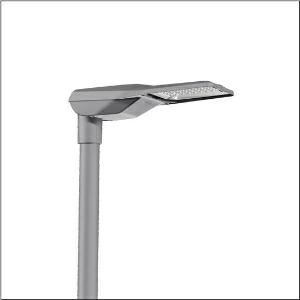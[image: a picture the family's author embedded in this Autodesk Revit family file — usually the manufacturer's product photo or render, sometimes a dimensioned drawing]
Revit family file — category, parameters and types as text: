
# Revit family: streetlight_sl_21_iq_mini___st1_0a_5xe2d31d08jb_a4dc
name_source: partatom
category: Lighting Fixtures
units: mm (PartAtom-declared; Revit-internal decimal feet)

## family parameters
Cut with Voids When Loaded = No
Host = Face
Light Source = No
Part Type = Normal
Room Calculation Point = No
Round Connector Dimension = Use Diameter
Shared = No

## types (1)
- --- (1 x LED, 10820 lm, 71.6 W, 3000K)
    Apparent Load = 72 VA
    CIE Flux Codes = 40 73 97 100 100
    Color Rendering = 70
    Color Temperature = 3000K
    Default Elevation = 1800 mm
    Description = Streetlight SL 21 iQ mini, mast luminaire, primary light control with lens, of PMMA, primary optical cover: cover, of toughened safety glass, transparent, light distribution: ST1.0a, light emission: direct distribution, primary light characteristic: asymmetric, installation type: post-top, side-entry, LED, High Power LED, rated luminous flux: 10.820lm, luminous efficacy: 151lm/W, light colour: 730, colour temperature: 3000K, control: Auto-Match, Temp-Guard, Lumen-Switch, Night-Set, Smart-Wire, Light-Fading, Desk-Remote (wireless, voltage-free reading and setting of iQ features in the workshop via application-optimized NFC function/RFID function), optimised constant luminous flux control (CLO 2.0), presetting dimming linear, mains connection: 220..240V, AC, 50/60Hz, start of lifetime: 72W, end of service life: 75W, reduction: 33W, luminaire housing, of diecast aluminium, powder-coated, Siteco® metallic grey (DB 702S), corrosivity category C5 mid according to DIN EN ISO 12944, please order mast flange separately, inclination adjustable: 0°, 5°, 10°, 15°, sealing non-destructively replaceable, multi-level sealing system, length: 628mm, width: 235mm, height: 110mm, mast flange for spigot size: 42mm (side-entry): 5XC10008XM4, 60/48mm (side-entry/post-top): 5XC10108XM2, 76/60mm (side-entry/post-top): 5XC10108XM1, protection rating (complete): IP66, insulation class (complete): insulation class II (safety insulation), certification: CE, ENEC, ENEC+, VDE, impact resistance: IK09, permissible operating ambient temperature for outdoor applications: -40..+50°C, standard-compliant lighting for roads and squares, packaging unit: 1 piece

Light Distribution: ST1.0a
    Height = 110 mm
    Lamp = 1 x LED
    Lamp Light Flux = 10820 lm
    Lamp Power = 71.6 W
    Lamp count = 1
    Length = 625 mm
    Luminous efficacy = 151 lm/W
    Manufacturer = Siteco
    ModVariant = No
    Model = 5XE2D31D08JB
    Number of Poles = 1
    OnlyDefault = Yes
    Power Factor = 1
    Product Name = Streetlight SL 21 iQ mini | ST1.0a
    Product group = mast luminaire | pylon top
    ProductGroupID = 6100
    Protection Class = Protection class II
    Protection Degree = IP 66
    RLX_Detail_Level = 1
    RLX_Emergency_Light_Flux = 0 lm
    RLX_Emergency_Type = 0
    RLX_Emergency_Type_DB = No
    RlxData = <blob elided: 92889 chars, md5=236975d0>
    Socket = socket
    Standby Power = 0 W
    System Light Flux = 10820 lm
    System Power = 72 W
    Type Comments = factory setting: luminous flux: 100 % | dim-lin: 254 | 746 mA
    Type Image = l_1003519.jpg
    URL = http://relux.com
    VarID = @adj_121975
    Voltage = 0 V
    Weight = 0.00 kg
    Width = 234 mm

## geometry (parser evidence)
native form markers: Blend x4, Sweep x11
no freeform markers — native parametric forms only
